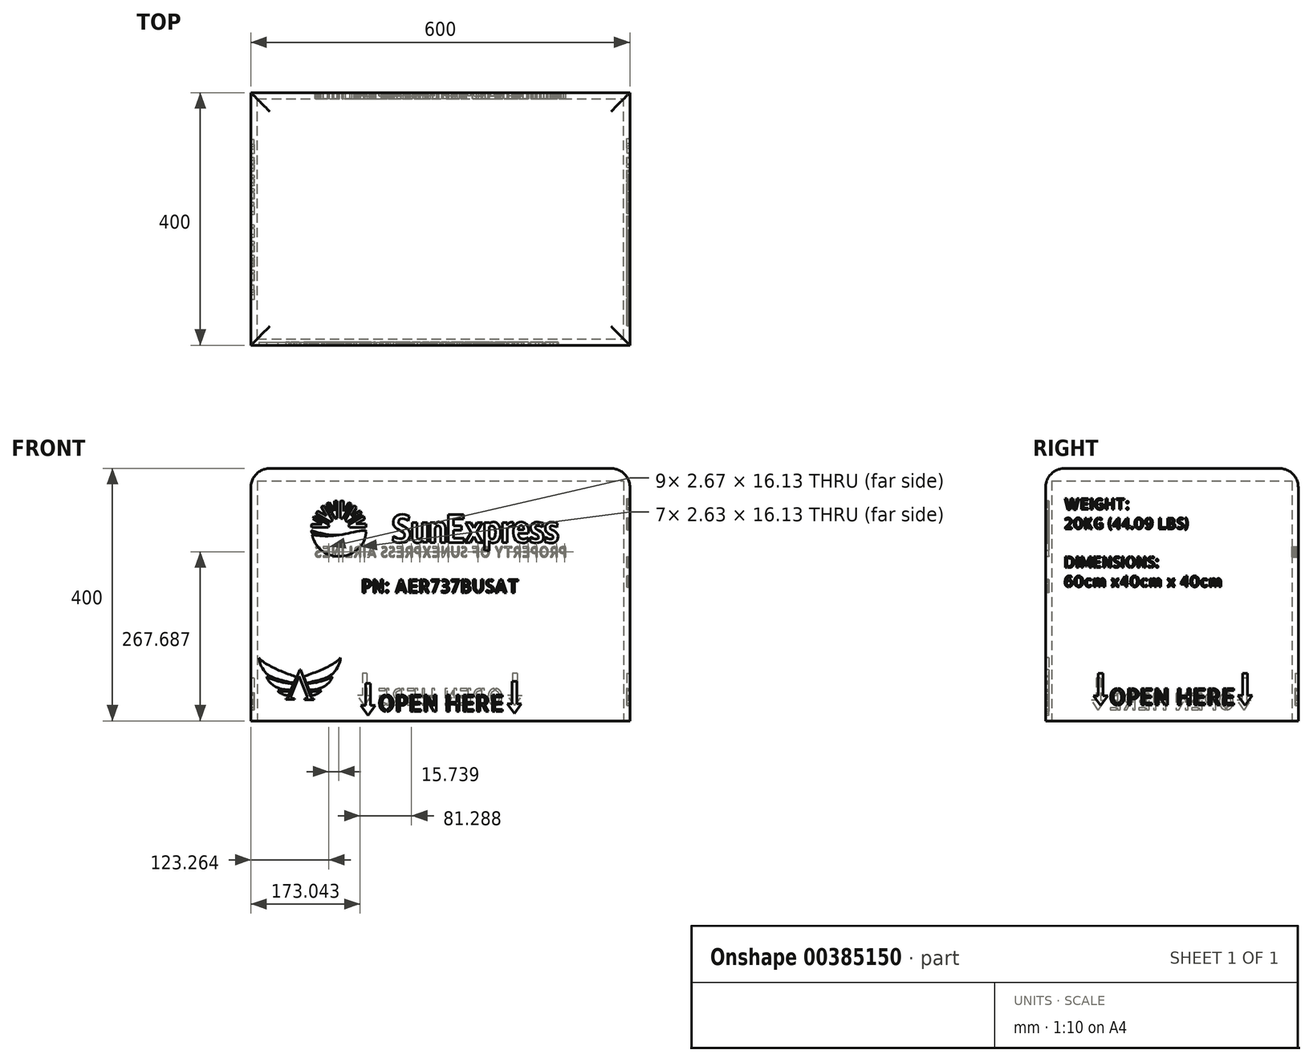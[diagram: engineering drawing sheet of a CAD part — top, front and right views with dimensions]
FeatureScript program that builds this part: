
annotation { "Feature Type Name" : "Feature", "Feature Type Description" : "" }
export const myFeature = defineFeature(function(context is Context, id is Id, definition is map)
    precondition{}
    {
        {
            var Q0;
            Q0=qCreatedBy(makeId("Top.planeOp"),FACE);
            var sketch = newSketch(context, id + "F0", { "sketchPlane" : qUnion([Q0])});
            skLineSegment(sketch, "E0.bottom", {"start": v(300, 200) * mm, "end": v(-300, 200) * mm});
            skLineSegment(sketch, "E0.top", {"start": v(300, -200) * mm, "end": v(-300, -200) * mm});
            skLineSegment(sketch, "E0.left", {"start": v(300, 200) * mm, "end": v(300, -200) * mm});
            skLineSegment(sketch, "E0.right", {"start": v(-300, 200) * mm, "end": v(-300, -200) * mm});
            skPoint(sketch, "E0.middle", {"position": v(0, 0) * mm});
            skSolve(sketch);
        }
        {
            var Q0;
            Q0=makeQuery(id+"F0.imprint","IMPRINT",FACE,{"disambiguationData":[TD([[makeQuery(id+"F0.imprint","IMPRINT",EDGE,{"derivedFrom":sQuery(id+"F0.wireOp",EDGE,"E0.bottom")}),1.0]])]});
            extrude(context, id + "F1", {"entities" : qUnion([Q0]), "oppositeDirection" : true, "depth" : 400 * mm});
        }
        {
            var Q0;
            Q0=makeQuery(id+"F1.opExtrude","CAP_FACE",FACE,{"disambiguationData":[OSD([sQuery(id+"F0.wireOp",EDGE,"E0.bottom"),sQuery(id+"F0.wireOp",EDGE,"E0.top"),sQuery(id+"F0.wireOp",EDGE,"E0.left"),sQuery(id+"F0.wireOp",EDGE,"E0.right")])],"isStart":false});
            var sketch = newSketch(context, id + "F2", { "sketchPlane" : qUnion([Q0])});
            skLineSegment(sketch, "E1.bottom", {"start": v(-290, 190) * mm, "end": v(290, 190) * mm});
            skLineSegment(sketch, "E1.top", {"start": v(-290, -190) * mm, "end": v(290, -190) * mm});
            skLineSegment(sketch, "E1.left", {"start": v(-290, 190) * mm, "end": v(-290, -190) * mm});
            skLineSegment(sketch, "E1.right", {"start": v(290, 190) * mm, "end": v(290, -190) * mm});
            skPoint(sketch, "E1.middle", {"position": v(0, 0) * mm});
            skSolve(sketch);
        }
        {
            var Q0;
            Q0 = qSketchRegion(id + "F2", true);
            extrude(context, id + "F3", {"entities" : qUnion([Q0]), "operationType" : NewBodyOperationType.REMOVE, "oppositeDirection" : true, "depth" : 380 * mm});
        }
        {
            var Q0;
            Q0=makeQuery(id+"F1.opExtrude","CAP_EDGE",EDGE,{"disambiguationData":[OSD([sQuery(id+"F0.wireOp",EDGE,"E0.right")])],"isStart":true});
            var Q1;
            Q1=makeQuery(id+"F1.opExtrude","CAP_EDGE",EDGE,{"disambiguationData":[OSD([sQuery(id+"F0.wireOp",EDGE,"E0.top")])],"isStart":true});
            var Q2;
            Q2=makeQuery(id+"F1.opExtrude","CAP_EDGE",EDGE,{"disambiguationData":[OSD([sQuery(id+"F0.wireOp",EDGE,"E0.left")])],"isStart":true});
            var Q3;
            Q3=makeQuery(id+"F1.opExtrude","CAP_EDGE",EDGE,{"disambiguationData":[OSD([sQuery(id+"F0.wireOp",EDGE,"E0.bottom")])],"isStart":true});
            fillet(context, id + "F4", {"entities" : qUnion([Q0, Q1, Q2, Q3]), "radius" : 30 * mm, "tangentPropagation" : true, "allowEdgeOverflow" : false});
        }
        {
            var Q0;
            Q0=makeQuery(id+"F1.opExtrude","SWEPT_FACE",FACE,{"disambiguationData":[OSD([sQuery(id+"F0.wireOp",EDGE,"E0.top")])]});
            var sketch = newSketch(context, id + "F5", { "sketchPlane" : qUnion([Q0])});
            skText(sketch, "E2", { "text": "PN: AER737BUSAT", "fontName": "AllertaStencil-Regular.ttf"});
            const initialGuessF5  = {"E2": [-0.12502, -0.19671, 1, 0, 0.02039]};
            skSetInitialGuess(sketch, initialGuessF5);
            skSolve(sketch);
        }
        {
            var Q0;
            Q0 = qSketchRegion(id + "F5", true);
            extrude(context, id + "F6", {"entities" : qUnion([Q0]), "operationType" : NewBodyOperationType.REMOVE, "oppositeDirection" : true, "depth" : 5 * mm});
        }
        {
            var Q0;
            Q0=makeQuery(id+"F1.opExtrude","SWEPT_FACE",FACE,{"disambiguationData":[OSD([sQuery(id+"F0.wireOp",EDGE,"E0.bottom")])]});
            var sketch = newSketch(context, id + "F7", { "sketchPlane" : qUnion([Q0])});
            skText(sketch, "E3", { "text": "PROPERTY OF SUNEXPRESS AIRLINES", "fontName": "AllertaStencil-Regular.ttf"});
            const initialGuessF7  = {"E3": [-0.2002, -0.14038, 1, 0, 0.01614]};
            skSetInitialGuess(sketch, initialGuessF7);
            skSolve(sketch);
        }
        {
            var Q0;
            Q0 = qSketchRegion(id + "F7", true);
            var Q1;
            Q1 = qConstructionFilter(qBodyType(qCreatedBy(id + "F7" ,EDGE), BodyType.WIRE), ConstructionObject.NO);
            extrude(context, id + "F8", {"entities" : qUnion([Q0]), "operationType" : NewBodyOperationType.REMOVE, "surfaceEntities" : qUnion([Q1]), "oppositeDirection" : true, "depth" : 25 * mm});
        }
        {
            var Q0;
            Q0=makeQuery(id+"F1.opExtrude","SWEPT_FACE",FACE,{"disambiguationData":[OSD([sQuery(id+"F0.wireOp",EDGE,"E0.left")])]});
            var sketch = newSketch(context, id + "F9", { "sketchPlane" : qUnion([Q0])});
            skText(sketch, "E4", { "text": "WEIGHT:\n20KG (44.09 LBS)\n\nDIMENSIONS:\n60cm x40cm x 40cm\n", "fontName": "AllertaStencil-Regular.ttf"});
            const initialGuessF9  = {"E4": [-0.17095, -0.0652, 1, 0, 0.01723]};
            skSetInitialGuess(sketch, initialGuessF9);
            skSolve(sketch);
        }
        {
            var Q0;
            Q0 = qSketchRegion(id + "F9", true);
            extrude(context, id + "F10", {"entities" : qUnion([Q0]), "operationType" : NewBodyOperationType.REMOVE, "oppositeDirection" : true, "depth" : 5 * mm});
        }
        {
            var Q0;
            Q0=makeQuery(id+"F1.opExtrude","SWEPT_FACE",FACE,{"disambiguationData":[OSD([sQuery(id+"F0.wireOp",EDGE,"E0.left")])]});
            var sketch = newSketch(context, id + "F11", { "sketchPlane" : qUnion([Q0])});
            skText(sketch, "E5", { "text": "OPEN HERE ", "fontName": "AllertaStencil-Regular.ttf"});
            const initialGuessF11  = {"E5": [-0.09974, -0.37501, 1, 0, 0.02609]};
            skSetInitialGuess(sketch, initialGuessF11);
            skSolve(sketch);
        }
        {
            var Q0;
            Q0 = qSketchRegion(id + "F11", true);
            extrude(context, id + "F12", {"entities" : qUnion([Q0]), "operationType" : NewBodyOperationType.REMOVE, "oppositeDirection" : true, "depth" : 5 * mm});
        }
        {
            var Q0;
            Q0=makeQuery(id+"F1.opExtrude","SWEPT_FACE",FACE,{"disambiguationData":[OSD([sQuery(id+"F0.wireOp",EDGE,"E0.bottom")])]});
            var sketch = newSketch(context, id + "F13", { "sketchPlane" : qUnion([Q0])});
            skText(sketch, "E6", { "text": "OPEN HERE", "fontName": "AllertaStencil-Regular.ttf"});
            const initialGuessF13  = {"E6": [-0.1, -0.375, 1, 0, 0.02609]};
            skSetInitialGuess(sketch, initialGuessF13);
            skSolve(sketch);
        }
        {
            var Q0;
            Q0 = qSketchRegion(id + "F13", true);
            var Q1;
            Q1 = qConstructionFilter(qBodyType(qCreatedBy(id + "F13" ,EDGE), BodyType.WIRE), ConstructionObject.NO);
            extrude(context, id + "F14", {"entities" : qUnion([Q0]), "operationType" : NewBodyOperationType.REMOVE, "surfaceEntities" : qUnion([Q1]), "oppositeDirection" : true, "depth" : 5 * mm});
        }
        {
            var Q0;
            Q0=makeQuery(id+"F1.opExtrude","SWEPT_FACE",FACE,{"disambiguationData":[OSD([sQuery(id+"F0.wireOp",EDGE,"E0.right")])]});
            var sketch = newSketch(context, id + "F15", { "sketchPlane" : qUnion([Q0])});
            skText(sketch, "E7", { "text": "OPEN HERE", "fontName": "AllertaStencil-Regular.ttf"});
            const initialGuessF15  = {"E7": [-0.09969, -0.38217, 1, 0, 0.02609]};
            skSetInitialGuess(sketch, initialGuessF15);
            skSolve(sketch);
        }
        {
            var Q0;
            Q0 = qSketchRegion(id + "F15", true);
            extrude(context, id + "F16", {"entities" : qUnion([Q0]), "operationType" : NewBodyOperationType.REMOVE, "oppositeDirection" : true, "depth" : 5 * mm});
        }
        {
            var Q0;
            Q0=makeQuery(id+"F1.opExtrude","SWEPT_FACE",FACE,{"disambiguationData":[OSD([sQuery(id+"F0.wireOp",EDGE,"E0.top")])]});
            var sketch = newSketch(context, id + "F17", { "sketchPlane" : qUnion([Q0])});
            skText(sketch, "E8", { "text": "OPEN HERE", "fontName": "AllertaStencil-Regular.ttf"});
            const initialGuessF17  = {"E8": [-0.09926, -0.38504, 1, 0, 0.02609]};
            skSetInitialGuess(sketch, initialGuessF17);
            skSolve(sketch);
        }
        {
            var Q0;
            Q0 = qSketchRegion(id + "F17", true);
            extrude(context, id + "F18", {"entities" : qUnion([Q0]), "operationType" : NewBodyOperationType.REMOVE, "oppositeDirection" : true, "depth" : 5 * mm});
        }
        {
            var Q0;
            Q0=makeQuery(id+"F1.opExtrude","SWEPT_FACE",FACE,{"disambiguationData":[OSD([sQuery(id+"F0.wireOp",EDGE,"E0.top")])]});
            var sketch = newSketch(context, id + "F19", { "sketchPlane" : qUnion([Q0])});
            skLineSegment(sketch, "E9", {"start": v(113.26, -337.65) * mm, "end": v(120.76, -337.65) * mm});
            skLineSegment(sketch, "E10", {"start": v(120.76, -337.65) * mm, "end": v(120.76, -372.65) * mm});
            skLineSegment(sketch, "E11", {"start": v(120.76, -372.65) * mm, "end": v(128.26, -372.65) * mm});
            skPoint(sketch, "E12.endSnap0", {"position": v(117, -337.65) * mm});
            skLineSegment(sketch, "E13", {"start": v(113.26, -337.65) * mm, "end": v(113.26, -372.65) * mm});
            skLineSegment(sketch, "E14", {"start": v(113.26, -372.65) * mm, "end": v(105.76, -372.65) * mm});
            skLineSegment(sketch, "E15", {"start": v(117, -388.42) * mm, "end": v(105.76, -372.65) * mm});
            skLineSegment(sketch, "E16", {"start": v(117, -388.42) * mm, "end": v(128.26, -372.65) * mm});
            skLineSegment(sketch, "E17", {"start": v(-118.37, -340.6) * mm, "end": v(-110.87, -340.6) * mm});
            skLineSegment(sketch, "E18", {"start": v(-110.87, -340.6) * mm, "end": v(-110.87, -375.6) * mm});
            skLineSegment(sketch, "E19", {"start": v(-110.87, -375.6) * mm, "end": v(-103.37, -375.6) * mm});
            skPoint(sketch, "E20.endSnap0", {"position": v(-114.62, -340.6) * mm});
            skLineSegment(sketch, "E21", {"start": v(-118.37, -340.6) * mm, "end": v(-118.37, -375.6) * mm});
            skLineSegment(sketch, "E22", {"start": v(-118.37, -375.6) * mm, "end": v(-125.87, -375.6) * mm});
            skLineSegment(sketch, "E23", {"start": v(-114.62, -391.38) * mm, "end": v(-125.87, -375.6) * mm});
            skLineSegment(sketch, "E24", {"start": v(-114.62, -391.38) * mm, "end": v(-103.37, -375.6) * mm});
            skSolve(sketch);
        }
        {
            var Q0;
            Q0=makeQuery(id+"F19.imprint","IMPRINT",FACE,{"disambiguationData":[TD([[makeQuery(id+"F19.imprint","IMPRINT",EDGE,{"derivedFrom":sQuery(id+"F19.wireOp",EDGE,"E9")}),-1.0]])]});
            var Q1;
            Q1=makeQuery(id+"F19.imprint","IMPRINT",FACE,{"disambiguationData":[TD([[makeQuery(id+"F19.imprint","IMPRINT",EDGE,{"derivedFrom":sQuery(id+"F19.wireOp",EDGE,"E17")}),-1.0]])]});
            extrude(context, id + "F20", {"entities" : qUnion([Q0, Q1]), "operationType" : NewBodyOperationType.REMOVE, "oppositeDirection" : true, "depth" : 5 * mm});
        }
        {
            var Q0;
            Q0=makeQuery(id+"F1.opExtrude","SWEPT_FACE",FACE,{"disambiguationData":[OSD([sQuery(id+"F0.wireOp",EDGE,"E0.left")])]});
            var sketch = newSketch(context, id + "F21", { "sketchPlane" : qUnion([Q0])});
            skLineSegment(sketch, "E25", {"start": v(112.16, -324.4) * mm, "end": v(119.66, -324.4) * mm});
            skLineSegment(sketch, "E26", {"start": v(119.66, -324.4) * mm, "end": v(119.66, -359.4) * mm});
            skLineSegment(sketch, "E27", {"start": v(119.66, -359.4) * mm, "end": v(127.16, -359.4) * mm});
            skPoint(sketch, "E28.endSnap0", {"position": v(115.91, -324.4) * mm});
            skLineSegment(sketch, "E29", {"start": v(112.16, -324.4) * mm, "end": v(112.16, -359.4) * mm});
            skLineSegment(sketch, "E30", {"start": v(112.16, -359.4) * mm, "end": v(104.66, -359.4) * mm});
            skLineSegment(sketch, "E31", {"start": v(115.91, -375.17) * mm, "end": v(104.66, -359.4) * mm});
            skLineSegment(sketch, "E32", {"start": v(115.91, -375.17) * mm, "end": v(127.16, -359.4) * mm});
            skLineSegment(sketch, "E33", {"start": v(-116.57, -324.94) * mm, "end": v(-109.07, -324.94) * mm});
            skLineSegment(sketch, "E34", {"start": v(-109.07, -324.94) * mm, "end": v(-109.07, -359.94) * mm});
            skLineSegment(sketch, "E35", {"start": v(-109.07, -359.94) * mm, "end": v(-101.57, -359.94) * mm});
            skPoint(sketch, "E36.endSnap0", {"position": v(-112.82, -324.94) * mm});
            skLineSegment(sketch, "E37", {"start": v(-116.57, -324.94) * mm, "end": v(-116.57, -359.94) * mm});
            skLineSegment(sketch, "E38", {"start": v(-116.57, -359.94) * mm, "end": v(-124.07, -359.94) * mm});
            skLineSegment(sketch, "E39", {"start": v(-112.82, -375.72) * mm, "end": v(-124.07, -359.94) * mm});
            skLineSegment(sketch, "E40", {"start": v(-112.82, -375.72) * mm, "end": v(-101.57, -359.94) * mm});
            skSolve(sketch);
        }
        {
            var Q0;
            Q0 = qSketchRegion(id + "F21", true);
            extrude(context, id + "F22", {"entities" : qUnion([Q0]), "operationType" : NewBodyOperationType.REMOVE, "oppositeDirection" : true, "depth" : 5 * mm});
        }
        {
            var Q0;
            Q0=makeQuery(id+"F1.opExtrude","SWEPT_FACE",FACE,{"disambiguationData":[OSD([sQuery(id+"F0.wireOp",EDGE,"E0.bottom")])]});
            var sketch = newSketch(context, id + "F23", { "sketchPlane" : qUnion([Q0])});
            skLineSegment(sketch, "E41", {"start": v(116.23, -324.57) * mm, "end": v(123.73, -324.57) * mm});
            skLineSegment(sketch, "E42", {"start": v(123.73, -324.57) * mm, "end": v(123.73, -359.57) * mm});
            skLineSegment(sketch, "E43", {"start": v(123.73, -359.57) * mm, "end": v(131.23, -359.57) * mm});
            skPoint(sketch, "E44.endSnap0", {"position": v(119.98, -324.57) * mm});
            skLineSegment(sketch, "E45", {"start": v(116.23, -324.57) * mm, "end": v(116.23, -359.57) * mm});
            skLineSegment(sketch, "E46", {"start": v(116.23, -359.57) * mm, "end": v(108.73, -359.57) * mm});
            skLineSegment(sketch, "E47", {"start": v(119.98, -375.34) * mm, "end": v(108.73, -359.57) * mm});
            skLineSegment(sketch, "E48", {"start": v(119.98, -375.34) * mm, "end": v(131.23, -359.57) * mm});
            skLineSegment(sketch, "E49", {"start": v(-121.59, -324.57) * mm, "end": v(-114.09, -324.57) * mm});
            skLineSegment(sketch, "E50", {"start": v(-114.09, -324.57) * mm, "end": v(-114.09, -359.57) * mm});
            skLineSegment(sketch, "E51", {"start": v(-114.09, -359.57) * mm, "end": v(-106.59, -359.57) * mm});
            skPoint(sketch, "E52.endSnap0", {"position": v(-117.84, -324.57) * mm});
            skLineSegment(sketch, "E53", {"start": v(-121.59, -324.57) * mm, "end": v(-121.59, -359.57) * mm});
            skLineSegment(sketch, "E54", {"start": v(-121.59, -359.57) * mm, "end": v(-129.09, -359.57) * mm});
            skLineSegment(sketch, "E55", {"start": v(-117.84, -375.34) * mm, "end": v(-129.09, -359.57) * mm});
            skLineSegment(sketch, "E56", {"start": v(-117.84, -375.34) * mm, "end": v(-106.59, -359.57) * mm});
            skSolve(sketch);
        }
        {
            var Q0;
            Q0 = qSketchRegion(id + "F23", true);
            extrude(context, id + "F24", {"entities" : qUnion([Q0]), "operationType" : NewBodyOperationType.REMOVE, "oppositeDirection" : true, "depth" : 5 * mm});
        }
        {
            var Q0;
            Q0=makeQuery(id+"F1.opExtrude","SWEPT_FACE",FACE,{"disambiguationData":[OSD([sQuery(id+"F0.wireOp",EDGE,"E0.right")])]});
            var sketch = newSketch(context, id + "F25", { "sketchPlane" : qUnion([Q0])});
            skLineSegment(sketch, "E57", {"start": v(112.6, -331.98) * mm, "end": v(120.1, -331.98) * mm});
            skLineSegment(sketch, "E58", {"start": v(120.1, -331.98) * mm, "end": v(120.1, -366.98) * mm});
            skLineSegment(sketch, "E59", {"start": v(120.1, -366.98) * mm, "end": v(127.6, -366.98) * mm});
            skPoint(sketch, "E60.endSnap0", {"position": v(116.35, -331.98) * mm});
            skLineSegment(sketch, "E61", {"start": v(112.6, -331.98) * mm, "end": v(112.6, -366.98) * mm});
            skLineSegment(sketch, "E62", {"start": v(112.6, -366.98) * mm, "end": v(105.1, -366.98) * mm});
            skLineSegment(sketch, "E63", {"start": v(116.35, -382.75) * mm, "end": v(105.1, -366.98) * mm});
            skLineSegment(sketch, "E64", {"start": v(116.35, -382.75) * mm, "end": v(127.6, -366.98) * mm});
            skLineSegment(sketch, "E65", {"start": v(-118.05, -331.98) * mm, "end": v(-110.55, -331.98) * mm});
            skLineSegment(sketch, "E66", {"start": v(-110.55, -331.98) * mm, "end": v(-110.55, -366.98) * mm});
            skLineSegment(sketch, "E67", {"start": v(-110.55, -366.98) * mm, "end": v(-103.05, -366.98) * mm});
            skPoint(sketch, "E68.endSnap0", {"position": v(-114.3, -331.98) * mm});
            skLineSegment(sketch, "E69", {"start": v(-118.05, -331.98) * mm, "end": v(-118.05, -366.98) * mm});
            skLineSegment(sketch, "E70", {"start": v(-118.05, -366.98) * mm, "end": v(-125.55, -366.98) * mm});
            skLineSegment(sketch, "E71", {"start": v(-114.3, -382.75) * mm, "end": v(-125.55, -366.98) * mm});
            skLineSegment(sketch, "E72", {"start": v(-114.3, -382.75) * mm, "end": v(-103.05, -366.98) * mm});
            skSolve(sketch);
        }
        {
            var Q0;
            Q0=makeQuery(id+"F25.imprint","IMPRINT",FACE,{"disambiguationData":[TD([[makeQuery(id+"F25.imprint","IMPRINT",EDGE,{"derivedFrom":sQuery(id+"F25.wireOp",EDGE,"E65")}),-1.0]])]});
            var Q1;
            Q1=makeQuery(id+"F25.imprint","IMPRINT",FACE,{"disambiguationData":[TD([[makeQuery(id+"F25.imprint","IMPRINT",EDGE,{"derivedFrom":sQuery(id+"F25.wireOp",EDGE,"E57")}),-1.0]])]});
            extrude(context, id + "F26", {"entities" : qUnion([Q0, Q1]), "operationType" : NewBodyOperationType.REMOVE, "oppositeDirection" : true, "depth" : 5 * mm});
        }
        {
            var Q0;
            Q0=makeQuery(id+"F1.opExtrude","SWEPT_FACE",FACE,{"disambiguationData":[OSD([sQuery(id+"F0.wireOp",EDGE,"E0.top")])]});
            var sketch = newSketch(context, id + "F27", { "sketchPlane" : qUnion([Q0])});
            skFitSpline(sketch, "E73", {"points": [v(-287.47, -300.17) * mm, v(-285.64, -307.65) * mm, v(-282.97, -314.34) * mm, v(-277.16, -323.03) * mm, v(-270.08, -328.64) * mm, v(-258.87, -333.26) * mm, v(-248.85, -336.14) * mm, v(-236.1, -339.08) * mm, v(-231.97, -339.77) * mm], "startDerivative": vector(14.73, -66.56) * mm, "endDerivative": vector(37.86, -4.5) * mm});
            skFitSpline(sketch, "E74", {"points": [v(-287.47, -300.17) * mm, v(-280.7, -306.24) * mm, v(-272.35, -311.5) * mm, v(-262.68, -316.6) * mm, v(-254.9, -320.18) * mm, v(-244.88, -324.1) * mm, v(-235, -327.89) * mm, v(-227.87, -330.32) * mm], "startDerivative": vector(46.83, -45.33) * mm, "endDerivative": vector(52.79, -17.03) * mm});
            skFitSpline(sketch, "E75", {"points": [v(-275.38, -329.68) * mm, v(-272.8, -334.93) * mm, v(-268.97, -339.85) * mm, v(-263.38, -344.43) * mm, v(-255.22, -348.27) * mm, v(-243.8, -350.68) * mm, v(-236.84, -351.02) * mm], "startDerivative": vector(16.29, -36.96) * mm, "endDerivative": vector(41.84, -0.26) * mm});
            skFitSpline(sketch, "E76", {"points": [v(-275.38, -329.68) * mm, v(-269.47, -332.6) * mm, v(-260.88, -335.85) * mm, v(-252.8, -338.18) * mm, v(-242.55, -340.18) * mm, v(-232.77, -341.62) * mm], "startDerivative": vector(32.04, -16.82) * mm, "endDerivative": vector(44.27, -6.3) * mm});
            skFitSpline(sketch, "E77", {"points": [v(-257.64, -352) * mm, v(-254.14, -355.29) * mm, v(-248.11, -358.3) * mm, v(-242.3, -359.56) * mm, v(-240.54, -359.56) * mm], "startDerivative": vector(12.37, -13.28) * mm, "endDerivative": vector(9.63, 0.61) * mm});
            skFitSpline(sketch, "E78", {"points": [v(-257.64, -352) * mm, v(-251.62, -352.83) * mm, v(-245.6, -353.32) * mm, v(-239.7, -353.4) * mm, v(-237.84, -353.32) * mm], "startDerivative": vector(21.45, -3.2) * mm, "endDerivative": vector(9.92, 0.53) * mm});
            skLineSegment(sketch, "E79", {"start": v(-204.23, -359.6) * mm, "end": v(-206.68, -353.37) * mm});
            skFitSpline(sketch, "E80", {"points": [v(-158.12, -300.1) * mm, v(-163.54, -305.05) * mm, v(-170.37, -309.88) * mm, v(-180.5, -315.3) * mm, v(-190.3, -319.9) * mm, v(-202.43, -324.61) * mm, v(-212.1, -328.38) * mm, v(-215.86, -330.03) * mm], "startDerivative": vector(-41.21, -39.44) * mm, "endDerivative": vector(-34.78, -15.75) * mm});
            skFitSpline(sketch, "E81", {"points": [v(-158.12, -300.1) * mm, v(-159.65, -307.64) * mm, v(-163.3, -315.9) * mm, v(-169.43, -324.38) * mm, v(-173.8, -327.56) * mm, v(-180.04, -330.98) * mm, v(-186.64, -333.69) * mm, v(-192.65, -335.46) * mm, v(-202.78, -337.81) * mm, v(-212.07, -339.68) * mm], "startDerivative": vector(-10.94, -69.54) * mm, "endDerivative": vector(-74.54, -14.42) * mm});
            skFitSpline(sketch, "E82", {"points": [v(-170.41, -330.03) * mm, v(-174.06, -336.2) * mm, v(-178.05, -340.9) * mm, v(-182.75, -344.54) * mm, v(-186.6, -346.57) * mm, v(-191.71, -348.68) * mm, v(-198.02, -350.29) * mm, v(-207.73, -350.7) * mm], "startDerivative": vector(-23.37, -42.5) * mm, "endDerivative": vector(-58.2, -0.2) * mm});
            skFitSpline(sketch, "E83", {"points": [v(-170.41, -330.03) * mm, v(-176.3, -332.7) * mm, v(-183.66, -335.43) * mm, v(-193.26, -338.38) * mm, v(-201.18, -339.78) * mm, v(-211.46, -341.24) * mm], "startDerivative": vector(-33.05, -15.61) * mm, "endDerivative": vector(-48.47, -6.89) * mm});
            skLineSegment(sketch, "E84.trimOffspring", {"start": v(-212.07, -339.68) * mm, "end": v(-215.86, -330.03) * mm});
            skFitSpline(sketch, "E85", {"points": [v(-188.1, -351.95) * mm, v(-193.65, -356.41) * mm, v(-199.9, -359.09) * mm, v(-204.23, -359.6) * mm], "startDerivative": vector(-14.5, -13.16) * mm, "endDerivative": vector(-14.58, -0.68) * mm});
            skFitSpline(sketch, "E86", {"points": [v(-188.1, -351.95) * mm, v(-194.55, -352.94) * mm, v(-199.4, -353.44) * mm, v(-204.23, -353.54) * mm, v(-206.68, -353.37) * mm], "startDerivative": vector(-22.43, -3.62) * mm, "endDerivative": vector(-12.06, 1.1) * mm});
            skLineSegment(sketch, "E87.trimOffspring", {"start": v(-207.73, -350.7) * mm, "end": v(-211.46, -341.24) * mm});
            skLineSegment(sketch, "E88", {"start": v(-240.54, -359.56) * mm, "end": v(-237.84, -353.32) * mm});
            skLineSegment(sketch, "E89.trimOffspring", {"start": v(-231.97, -339.77) * mm, "end": v(-227.87, -330.32) * mm});
            skLineSegment(sketch, "E90.trimOffspring", {"start": v(-236.84, -351.02) * mm, "end": v(-232.77, -341.62) * mm});
            skLineSegment(sketch, "E91", {"start": v(-239.23, -360.06) * mm, "end": v(-222.17, -318.74) * mm});
            skLineSegment(sketch, "E92", {"start": v(-222.17, -318.74) * mm, "end": v(-221.15, -318.74) * mm});
            skLineSegment(sketch, "E93", {"start": v(-221.15, -318.74) * mm, "end": v(-205.95, -360) * mm});
            skLineSegment(sketch, "E94", {"start": v(-223.7, -328.86) * mm, "end": v(-236.54, -360.55) * mm});
            skLineSegment(sketch, "E95", {"start": v(-223.7, -328.86) * mm, "end": v(-211.3, -360.72) * mm});
            skLineSegment(sketch, "E96", {"start": v(-244.84, -364.89) * mm, "end": v(-244.84, -366.15) * mm});
            skLineSegment(sketch, "E97", {"start": v(-244.84, -366.15) * mm, "end": v(-230.97, -366.15) * mm});
            skLineSegment(sketch, "E98", {"start": v(-230.97, -366.15) * mm, "end": v(-230.9, -364.89) * mm});
            skLineSegment(sketch, "E99", {"start": v(-214.7, -364.96) * mm, "end": v(-214.7, -366.29) * mm});
            skLineSegment(sketch, "E100", {"start": v(-214.7, -366.29) * mm, "end": v(-200.13, -366.29) * mm});
            skLineSegment(sketch, "E101", {"start": v(-200.13, -366.29) * mm, "end": v(-200.13, -364.68) * mm});
            skFitSpline(sketch, "E102", {"points": [v(-239.23, -360.06) * mm, v(-240.36, -362.22) * mm, v(-241.97, -363.9) * mm, v(-244.84, -364.89) * mm], "startDerivative": vector(-3.24, -6.88) * mm, "endDerivative": vector(-8.66, -2.08) * mm});
            skFitSpline(sketch, "E103", {"points": [v(-236.54, -360.55) * mm, v(-236.79, -361.65) * mm, v(-236.2, -363.16) * mm, v(-234.36, -364.18) * mm, v(-230.9, -364.89) * mm], "startDerivative": vector(-2.04, -5.52) * mm, "endDerivative": vector(11.11, -1.85) * mm});
            skFitSpline(sketch, "E104", {"points": [v(-211.3, -360.72) * mm, v(-211, -362.04) * mm, v(-210.97, -363.27) * mm, v(-211.7, -364.16) * mm, v(-213.24, -364.6) * mm, v(-214.7, -364.96) * mm], "startDerivative": vector(1.59, -6.6) * mm, "endDerivative": vector(-6.8, -1.78) * mm});
            skFitSpline(sketch, "E105", {"points": [v(-205.95, -360) * mm, v(-205.25, -361.45) * mm, v(-204.43, -362.95) * mm, v(-203.19, -364.19) * mm, v(-201.75, -364.54) * mm, v(-200.13, -364.68) * mm], "startDerivative": vector(3.47, -7.3) * mm, "endDerivative": vector(8.17, -0.63) * mm});
            skLineSegment(sketch, "E106", {"start": v(-201, -80.25) * mm, "end": v(-201.3, -79.66) * mm});
            skLineSegment(sketch, "E107", {"start": v(-201.3, -79.66) * mm, "end": v(-199.65, -76.18) * mm});
            skLineSegment(sketch, "E108", {"start": v(-199.65, -76.18) * mm, "end": v(-198.6, -76.1) * mm});
            skLineSegment(sketch, "E109", {"start": v(-198.6, -76.1) * mm, "end": v(-176.66, -88.87) * mm});
            skLineSegment(sketch, "E110", {"start": v(-176.66, -88.87) * mm, "end": v(-176.17, -89.8) * mm});
            skLineSegment(sketch, "E111", {"start": v(-176.17, -89.8) * mm, "end": v(-176.81, -92.38) * mm});
            skLineSegment(sketch, "E112", {"start": v(-176.81, -92.38) * mm, "end": v(-177.45, -93.23) * mm});
            skLineSegment(sketch, "E113", {"start": v(-177.45, -93.23) * mm, "end": v(-203.22, -93.23) * mm});
            skLineSegment(sketch, "E114", {"start": v(-203.22, -93.23) * mm, "end": v(-203.96, -92.43) * mm});
            skLineSegment(sketch, "E115", {"start": v(-203.96, -92.43) * mm, "end": v(-203.96, -89.06) * mm});
            skLineSegment(sketch, "E116", {"start": v(-203.96, -89.06) * mm, "end": v(-203.17, -88.22) * mm});
            skLineSegment(sketch, "E117", {"start": v(-203.17, -88.22) * mm, "end": v(-187.81, -88.22) * mm});
            skLineSegment(sketch, "E118", {"start": v(-187.81, -88.22) * mm, "end": v(-201, -80.25) * mm});
            skLineSegment(sketch, "E119", {"start": v(-196.59, -71.78) * mm, "end": v(-174.59, -84.66) * mm});
            skLineSegment(sketch, "E120", {"start": v(-174.59, -84.66) * mm, "end": v(-173.34, -84.57) * mm});
            skLineSegment(sketch, "E121", {"start": v(-173.34, -84.57) * mm, "end": v(-171.25, -82.74) * mm});
            skLineSegment(sketch, "E122", {"start": v(-171.25, -82.74) * mm, "end": v(-171.17, -81.82) * mm});
            skLineSegment(sketch, "E123", {"start": v(-171.17, -81.82) * mm, "end": v(-183.76, -59.6) * mm});
            skLineSegment(sketch, "E124", {"start": v(-183.76, -59.6) * mm, "end": v(-184.7, -58.88) * mm});
            skLineSegment(sketch, "E125", {"start": v(-184.7, -58.88) * mm, "end": v(-188, -61.06) * mm});
            skLineSegment(sketch, "E126", {"start": v(-188, -61.06) * mm, "end": v(-188, -62) * mm});
            skLineSegment(sketch, "E127", {"start": v(-188, -62) * mm, "end": v(-180.73, -75.19) * mm});
            skLineSegment(sketch, "E128", {"start": v(-180.73, -75.19) * mm, "end": v(-193.46, -67.84) * mm});
            skLineSegment(sketch, "E129", {"start": v(-193.46, -67.84) * mm, "end": v(-194.54, -67.93) * mm});
            skLineSegment(sketch, "E130", {"start": v(-194.54, -67.93) * mm, "end": v(-196.67, -70.67) * mm});
            skLineSegment(sketch, "E131", {"start": v(-196.67, -70.67) * mm, "end": v(-196.59, -71.78) * mm});
            skLineSegment(sketch, "E132", {"start": v(-179.98, -57.34) * mm, "end": v(-166.93, -79.75) * mm});
            skLineSegment(sketch, "E133", {"start": v(-166.93, -79.75) * mm, "end": v(-166.18, -79.75) * mm});
            skLineSegment(sketch, "E134", {"start": v(-166.18, -79.75) * mm, "end": v(-163.72, -79.13) * mm});
            skLineSegment(sketch, "E135", {"start": v(-163.72, -79.13) * mm, "end": v(-163.1, -78.42) * mm});
            skLineSegment(sketch, "E136", {"start": v(-163.1, -78.42) * mm, "end": v(-163.1, -52.55) * mm});
            skLineSegment(sketch, "E137", {"start": v(-163.1, -52.55) * mm, "end": v(-163.62, -51.51) * mm});
            skLineSegment(sketch, "E138", {"start": v(-163.62, -51.51) * mm, "end": v(-167.44, -51.79) * mm});
            skLineSegment(sketch, "E139", {"start": v(-167.44, -51.79) * mm, "end": v(-168.14, -52.58) * mm});
            skLineSegment(sketch, "E140", {"start": v(-168.14, -52.58) * mm, "end": v(-168.14, -67.7) * mm});
            skLineSegment(sketch, "E141", {"start": v(-168.14, -67.7) * mm, "end": v(-175.46, -54.67) * mm});
            skLineSegment(sketch, "E142", {"start": v(-175.46, -54.67) * mm, "end": v(-176.16, -54.23) * mm});
            skLineSegment(sketch, "E143", {"start": v(-176.16, -54.23) * mm, "end": v(-179.92, -55.86) * mm});
            skLineSegment(sketch, "E144", {"start": v(-179.98, -57.34) * mm, "end": v(-179.92, -55.86) * mm});
            skLineSegment(sketch, "E145", {"start": v(-158.5, -78.26) * mm, "end": v(-158.5, -52.33) * mm});
            skLineSegment(sketch, "E146", {"start": v(-158.5, -52.33) * mm, "end": v(-157.7, -51.37) * mm});
            skLineSegment(sketch, "E147", {"start": v(-157.7, -51.37) * mm, "end": v(-154.16, -51.58) * mm});
            skLineSegment(sketch, "E148", {"start": v(-154.16, -51.58) * mm, "end": v(-153.32, -52.53) * mm});
            skLineSegment(sketch, "E149", {"start": v(-153.32, -52.53) * mm, "end": v(-153.32, -68.05) * mm});
            skLineSegment(sketch, "E150", {"start": v(-153.32, -68.05) * mm, "end": v(-145.83, -54.56) * mm});
            skLineSegment(sketch, "E151", {"start": v(-145.83, -54.56) * mm, "end": v(-145.05, -54.18) * mm});
            skLineSegment(sketch, "E152", {"start": v(-145.05, -54.18) * mm, "end": v(-141.48, -55.96) * mm});
            skLineSegment(sketch, "E153", {"start": v(-141.48, -55.96) * mm, "end": v(-141.2, -56.74) * mm});
            skLineSegment(sketch, "E154", {"start": v(-141.2, -56.74) * mm, "end": v(-154.5, -79.68) * mm});
            skLineSegment(sketch, "E155", {"start": v(-154.5, -79.68) * mm, "end": v(-155.12, -79.85) * mm});
            skLineSegment(sketch, "E156", {"start": v(-155.12, -79.85) * mm, "end": v(-157.67, -79.26) * mm});
            skLineSegment(sketch, "E157", {"start": v(-157.67, -79.26) * mm, "end": v(-158.5, -78.26) * mm});
            skLineSegment(sketch, "E158", {"start": v(-137.45, -59.32) * mm, "end": v(-150.2, -81.53) * mm});
            skLineSegment(sketch, "E159", {"start": v(-150.2, -81.53) * mm, "end": v(-150.12, -82.69) * mm});
            skLineSegment(sketch, "E160", {"start": v(-150.12, -82.69) * mm, "end": v(-147.98, -84.82) * mm});
            skLineSegment(sketch, "E161", {"start": v(-147.98, -84.82) * mm, "end": v(-147.07, -84.9) * mm});
            skLineSegment(sketch, "E162", {"start": v(-147.07, -84.9) * mm, "end": v(-125.14, -72.14) * mm});
            skLineSegment(sketch, "E163", {"start": v(-125.14, -72.14) * mm, "end": v(-124.4, -71.05) * mm});
            skLineSegment(sketch, "E164", {"start": v(-124.4, -71.05) * mm, "end": v(-126.65, -67.72) * mm});
            skLineSegment(sketch, "E165", {"start": v(-126.65, -67.72) * mm, "end": v(-127.94, -67.62) * mm});
            skLineSegment(sketch, "E166", {"start": v(-127.94, -67.62) * mm, "end": v(-141.19, -75.47) * mm});
            skLineSegment(sketch, "E167", {"start": v(-141.19, -75.47) * mm, "end": v(-133.16, -62.19) * mm});
            skLineSegment(sketch, "E168", {"start": v(-133.16, -62.19) * mm, "end": v(-133.3, -60.9) * mm});
            skLineSegment(sketch, "E169", {"start": v(-133.3, -60.9) * mm, "end": v(-136.5, -58.86) * mm});
            skLineSegment(sketch, "E170", {"start": v(-136.5, -58.86) * mm, "end": v(-137.44, -59.31) * mm});
            skLineSegment(sketch, "E171", {"start": v(-122.82, -75.84) * mm, "end": v(-144.9, -88.76) * mm});
            skLineSegment(sketch, "E172", {"start": v(-144.9, -88.76) * mm, "end": v(-145.4, -89.93) * mm});
            skLineSegment(sketch, "E173", {"start": v(-145.4, -89.93) * mm, "end": v(-144.66, -92.5) * mm});
            skLineSegment(sketch, "E174", {"start": v(-144.66, -92.5) * mm, "end": v(-143.49, -93.26) * mm});
            skLineSegment(sketch, "E175", {"start": v(-143.49, -93.26) * mm, "end": v(-118.32, -93.26) * mm});
            skLineSegment(sketch, "E176", {"start": v(-118.32, -93.26) * mm, "end": v(-117.54, -92.52) * mm});
            skLineSegment(sketch, "E177", {"start": v(-117.54, -92.52) * mm, "end": v(-117.54, -88.87) * mm});
            skLineSegment(sketch, "E178", {"start": v(-117.54, -88.87) * mm, "end": v(-118.57, -88.1) * mm});
            skLineSegment(sketch, "E179", {"start": v(-118.57, -88.1) * mm, "end": v(-133.49, -88.1) * mm});
            skLineSegment(sketch, "E180", {"start": v(-133.49, -88.1) * mm, "end": v(-120.32, -80.5) * mm});
            skLineSegment(sketch, "E181", {"start": v(-120.32, -80.5) * mm, "end": v(-119.99, -79.68) * mm});
            skLineSegment(sketch, "E182", {"start": v(-119.99, -79.68) * mm, "end": v(-121.66, -75.93) * mm});
            skLineSegment(sketch, "E183", {"start": v(-121.66, -75.93) * mm, "end": v(-122.82, -75.84) * mm});
            skFitSpline(sketch, "E184", {"points": [v(-202.88, -105.5) * mm, v(-201.76, -110) * mm, v(-199.52, -115.46) * mm, v(-194.75, -123.03) * mm, v(-187.04, -130.88) * mm, v(-179.34, -135.5) * mm, v(-168.96, -138.73) * mm, v(-156.91, -139.43) * mm, v(-143.74, -136.34) * mm, v(-133.79, -130.46) * mm, v(-125.8, -122.6) * mm, v(-120.75, -114.06) * mm, v(-118.37, -105.5) * mm, v(-117.39, -99.9) * mm], "startDerivative": vector(17.85, -81.63) * mm, "endDerivative": vector(14.13, 87.9) * mm});
            skFitSpline(sketch, "E185", {"points": [v(-117.39, -99.9) * mm, v(-117.75, -99.07) * mm, v(-118.45, -98.57) * mm, v(-120.1, -98.48) * mm, v(-124.23, -98.62) * mm, v(-127.68, -98.92) * mm, v(-134.57, -100.24) * mm, v(-142, -101.94) * mm, v(-147.26, -103.08) * mm, v(-153.8, -104.52) * mm, v(-162.96, -106.15) * mm, v(-168.76, -106.85) * mm, v(-173.91, -107.15) * mm, v(-181.25, -107.3) * mm, v(-186.15, -107.05) * mm, v(-190.42, -106.84) * mm, v(-194.22, -106.37) * mm, v(-197.63, -105.8) * mm, v(-200.82, -105.36) * mm, v(-201.97, -105.2) * mm, v(-202.45, -105.15) * mm, v(-202.73, -105.25) * mm, v(-202.88, -105.35) * mm, v(-202.88, -105.5) * mm], "startDerivative": vector(-11.95, 38.51) * mm, "endDerivative": vector(2.6, -17.78) * mm});
            skFitSpline(sketch, "E186", {"points": [v(-199.86, -114.76) * mm, v(-195.32, -114.91) * mm, v(-192.21, -114.87) * mm, v(-188.48, -114.7) * mm, v(-183.43, -114.5) * mm, v(-177.98, -113.96) * mm, v(-170.85, -113.29) * mm, v(-162.52, -112.33) * mm, v(-156.02, -111.54) * mm, v(-151.73, -111.08) * mm, v(-145.64, -110.66) * mm, v(-140.77, -110.37) * mm, v(-133.8, -110.08) * mm, v(-128.27, -110.08) * mm, v(-122.93, -110.5) * mm, v(-119.73, -111.11) * mm], "startDerivative": vector(77.16, -3.3) * mm, "endDerivative": vector(56.56, -12.62) * mm});
            skFitSpline(sketch, "E187", {"points": [v(-204.13, -99.36) * mm, v(-203.92, -101.07) * mm, v(-203.87, -101.33) * mm, v(-203.73, -101.57) * mm, v(-203.45, -101.79) * mm, v(-200.27, -102.62) * mm, v(-195.9, -103.63) * mm, v(-191.66, -104.46) * mm, v(-187.66, -105.15) * mm, v(-183.4, -105.8) * mm, v(-178.8, -106.08) * mm, v(-173.93, -106.37) * mm, v(-168.9, -106.19) * mm, v(-161.17, -105.65) * mm], "startDerivative": vector(4.48, -35.82) * mm, "endDerivative": vector(65.82, 4.7) * mm});
            skFitSpline(sketch, "E188", {"points": [v(-204.13, -99.36) * mm, v(-204.13, -99.03) * mm, v(-203.92, -98.57) * mm, v(-203.48, -98.3) * mm, v(-202.98, -98.35) * mm, v(-201.97, -98.7) * mm, v(-200.13, -99.44) * mm, v(-196.97, -100.56) * mm, v(-192.97, -101.8) * mm, v(-188.96, -102.76) * mm, v(-183.01, -103.95) * mm, v(-178.5, -104.8) * mm, v(-173.94, -105.36) * mm, v(-171.34, -105.63) * mm, v(-168.82, -105.75) * mm, v(-165.72, -105.73) * mm, v(-161.17, -105.65) * mm], "startDerivative": vector(-1.3, 13.7) * mm, "endDerivative": vector(55.49, 1.12) * mm});
            skLineSegment(sketch, "E189", {"start": v(-50.9, -83.27) * mm, "end": v(-49.42, -75.8) * mm});
            skLineSegment(sketch, "E190", {"start": v(-74.47, -107.4) * mm, "end": v(-75.38, -115.24) * mm});
            skLineSegment(sketch, "E191", {"start": v(-44.91, -108.52) * mm, "end": v(-44.91, -85.81) * mm});
            skLineSegment(sketch, "E192", {"start": v(-44.91, -85.81) * mm, "end": v(-37.35, -85.81) * mm});
            skLineSegment(sketch, "E193", {"start": v(-20.83, -85.81) * mm, "end": v(-20.83, -117.24) * mm});
            skLineSegment(sketch, "E194", {"start": v(-20.83, -117.24) * mm, "end": v(-28.11, -117.24) * mm});
            skLineSegment(sketch, "E195", {"start": v(-28.11, -117.24) * mm, "end": v(-28.11, -113.62) * mm});
            skLineSegment(sketch, "E196", {"start": v(-37.35, -85.81) * mm, "end": v(-37.35, -108.52) * mm});
            skLineSegment(sketch, "E197", {"start": v(-28.51, -85.81) * mm, "end": v(-28.51, -107.83) * mm});
            skLineSegment(sketch, "E198.trimOffspring", {"start": v(-28.51, -85.81) * mm, "end": v(-20.83, -85.81) * mm});
            skLineSegment(sketch, "E199", {"start": v(-16.13, -117.58) * mm, "end": v(-8.7, -117.58) * mm});
            skLineSegment(sketch, "E200", {"start": v(-16.13, -117.58) * mm, "end": v(-16.13, -85.81) * mm});
            skLineSegment(sketch, "E201", {"start": v(-8.7, -117.58) * mm, "end": v(-8.7, -95.34) * mm});
            skLineSegment(sketch, "E202", {"start": v(0.23, -117.58) * mm, "end": v(0.23, -95.57) * mm});
            skLineSegment(sketch, "E203", {"start": v(8.03, -117.58) * mm, "end": v(8.03, -95.8) * mm});
            skLineSegment(sketch, "E204", {"start": v(12.75, -117.58) * mm, "end": v(12.75, -73.3) * mm});
            skLineSegment(sketch, "E205", {"start": v(12.75, -73.3) * mm, "end": v(36.33, -73.3) * mm});
            skLineSegment(sketch, "E206", {"start": v(36.33, -73.3) * mm, "end": v(36.33, -80.13) * mm});
            skLineSegment(sketch, "E207", {"start": v(36.33, -80.13) * mm, "end": v(20.82, -80.13) * mm});
            skLineSegment(sketch, "E208", {"start": v(20.82, -80.13) * mm, "end": v(20.82, -90.8) * mm});
            skLineSegment(sketch, "E209", {"start": v(20.82, -110.61) * mm, "end": v(37.05, -110.61) * mm});
            skLineSegment(sketch, "E210", {"start": v(37.05, -110.61) * mm, "end": v(37.05, -117.58) * mm});
            skLineSegment(sketch, "E211", {"start": v(20.82, -90.8) * mm, "end": v(33.19, -90.8) * mm});
            skLineSegment(sketch, "E212", {"start": v(33.19, -90.8) * mm, "end": v(33.19, -98.13) * mm});
            skLineSegment(sketch, "E213", {"start": v(33.19, -98.13) * mm, "end": v(20.82, -98.13) * mm});
            skLineSegment(sketch, "E214", {"start": v(39.8, -85.81) * mm, "end": v(48.94, -101.48) * mm});
            skLineSegment(sketch, "E215", {"start": v(48.24, -85.81) * mm, "end": v(53.28, -94.3) * mm});
            skLineSegment(sketch, "E216", {"start": v(58.42, -85.81) * mm, "end": v(53.28, -94.3) * mm});
            skLineSegment(sketch, "E217", {"start": v(66.62, -85.81) * mm, "end": v(57.3, -101.08) * mm});
            skLineSegment(sketch, "E218", {"start": v(69.47, -85.81) * mm, "end": v(69.47, -130.56) * mm});
            skLineSegment(sketch, "E219", {"start": v(69.47, -130.56) * mm, "end": v(77.25, -130.56) * mm});
            skLineSegment(sketch, "E220", {"start": v(77.25, -130.56) * mm, "end": v(77.25, -114.65) * mm});
            skLineSegment(sketch, "E221", {"start": v(98.22, -117.58) * mm, "end": v(98.22, -85.81) * mm});
            skFitSpline(sketch, "E222", {"points": [v(-49.42, -75.8) * mm, v(-51.45, -74.53) * mm, v(-54.78, -73.34) * mm, v(-58.99, -72.6) * mm, v(-63.75, -72.85) * mm, v(-67.01, -73.83) * mm, v(-70.16, -75.8) * mm, v(-73.21, -79.12) * mm, v(-74.5, -82.84) * mm, v(-74.47, -87.22) * mm, v(-73.84, -90.3) * mm, v(-72.1, -93.2) * mm, v(-69.78, -95.27) * mm, v(-68.03, -96.5) * mm, v(-65.08, -98.15) * mm, v(-61.16, -99.97) * mm, v(-58.18, -102) * mm, v(-57.06, -103.26) * mm, v(-56.57, -105.2) * mm, v(-56.67, -107.96) * mm, v(-58, -109.71) * mm, v(-60.18, -110.94) * mm, v(-63.09, -111.5) * mm, v(-66.77, -111.11) * mm, v(-69.99, -109.89) * mm, v(-72.37, -108.7) * mm, v(-74.47, -107.4) * mm], "startDerivative": vector(-56.48, 39.34) * mm, "endDerivative": vector(-61.2, 39.37) * mm});
            skPoint(sketch, "E223.13.internal.snap0", {"position": v(-44.91, -97.16) * mm});
            skFitSpline(sketch, "E223", {"points": [v(-75.38, -115.24) * mm, v(-73.1, -116.33) * mm, v(-70.58, -117.2) * mm, v(-66.59, -118.12) * mm, v(-63.4, -118.12) * mm, v(-59.3, -117.75) * mm, v(-54.8, -116.37) * mm, v(-52.11, -114.47) * mm, v(-50.07, -112.26) * mm, v(-48.8, -109.71) * mm, v(-48.17, -105.6) * mm, v(-48.23, -102.18) * mm, v(-49.14, -99.32) * mm, v(-50.38, -97.16) * mm, v(-52.65, -95.02) * mm, v(-54.83, -93.64) * mm, v(-58, -92.04) * mm, v(-61.02, -90.54) * mm, v(-63.7, -88.98) * mm, v(-65.05, -87.95) * mm, v(-66.23, -86.36) * mm, v(-66.3, -83.53) * mm, v(-65, -81.26) * mm, v(-63.08, -80) * mm, v(-60.22, -79.67) * mm, v(-57.75, -79.88) * mm, v(-55.12, -80.7) * mm, v(-53.09, -81.8) * mm, v(-50.9, -83.27) * mm], "startDerivative": vector(69.03, -35.17) * mm, "endDerivative": vector(65.6, -46.07) * mm});
            skFitSpline(sketch, "E224", {"points": [v(-44.91, -108.52) * mm, v(-44.7, -110.95) * mm, v(-43.83, -113.66) * mm, v(-42.12, -116.15) * mm, v(-40.35, -117.32) * mm, v(-38.2, -118) * mm, v(-36.56, -118.08) * mm, v(-33.99, -118.06) * mm, v(-31.95, -117.3) * mm, v(-29.68, -115.55) * mm, v(-28.11, -113.62) * mm], "startDerivative": vector(1.16, -24) * mm, "endDerivative": vector(13.97, 19.41) * mm});
            skFitSpline(sketch, "E225", {"points": [v(-37.35, -108.52) * mm, v(-36.93, -109.52) * mm, v(-36.06, -110.87) * mm, v(-34.51, -111.75) * mm, v(-32.38, -111.76) * mm, v(-30.9, -110.92) * mm, v(-29.17, -109.01) * mm, v(-28.51, -107.83) * mm], "startDerivative": vector(3.25, -8.47) * mm, "endDerivative": vector(4.12, 8.7) * mm});
            skFitSpline(sketch, "E226", {"points": [v(-8.7, -95.34) * mm, v(-8.25, -94.3) * mm, v(-6.69, -92.39) * mm, v(-4.9, -91.24) * mm, v(-3.42, -91.15) * mm, v(-1.86, -91.56) * mm, v(-0.59, -92.8) * mm, v(0, -94.27) * mm, v(0.23, -95.57) * mm], "startDerivative": vector(3.22, 9.32) * mm, "endDerivative": vector(1.58, -11.57) * mm});
            skFitSpline(sketch, "E227", {"points": [v(-8.7, -88.92) * mm, v(-7.83, -87.82) * mm, v(-6.13, -86.33) * mm, v(-4.26, -85.3) * mm, v(-3.07, -84.92) * mm, v(-1.76, -84.93) * mm, v(0.62, -84.97) * mm, v(2.03, -85.33) * mm, v(4.12, -86.3) * mm, v(5.67, -87.78) * mm, v(6.97, -90.05) * mm, v(7.73, -92.71) * mm, v(8.03, -95.8) * mm], "startDerivative": vector(11.21, 15.5) * mm, "endDerivative": vector(1.97, -30.63) * mm});
            skLineSegment(sketch, "E228.trimOffspring", {"start": v(-8.7, -88.92) * mm, "end": v(-8.7, -85.81) * mm});
            skLineSegment(sketch, "E229.trimOffspring", {"start": v(0.23, -117.58) * mm, "end": v(8.03, -117.58) * mm});
            skLineSegment(sketch, "E230.trimOffspring", {"start": v(39.8, -85.81) * mm, "end": v(48.24, -85.81) * mm});
            skLineSegment(sketch, "E231.trimOffspring", {"start": v(12.75, -117.58) * mm, "end": v(37.05, -117.58) * mm});
            skLineSegment(sketch, "E232.trimOffspring", {"start": v(20.82, -98.13) * mm, "end": v(20.82, -110.61) * mm});
            skLineSegment(sketch, "E233.trimOffspring", {"start": v(39.2, -117.58) * mm, "end": v(47.21, -117.58) * mm});
            skLineSegment(sketch, "E234.trimOffspring", {"start": v(52.9, -108.27) * mm, "end": v(58.32, -117.58) * mm});
            skLineSegment(sketch, "E235.trimOffspring", {"start": v(48.94, -101.48) * mm, "end": v(39.2, -117.58) * mm});
            skLineSegment(sketch, "E236.trimOffspring", {"start": v(57.3, -101.08) * mm, "end": v(67.08, -117.58) * mm});
            skLineSegment(sketch, "E237.trimOffspring", {"start": v(52.9, -108.27) * mm, "end": v(47.21, -117.58) * mm});
            skLineSegment(sketch, "E238.trimOffspring", {"start": v(58.42, -85.81) * mm, "end": v(66.62, -85.81) * mm});
            skLineSegment(sketch, "E239.trimOffspring", {"start": v(58.32, -117.58) * mm, "end": v(67.08, -117.58) * mm});
            skFitSpline(sketch, "E240", {"points": [v(77.25, -93.72) * mm, v(78.24, -92.24) * mm, v(79.84, -91.25) * mm, v(81.98, -91.16) * mm, v(84.03, -91.88) * mm, v(85.55, -93.52) * mm, v(86.46, -95.65) * mm, v(86.92, -98.32) * mm, v(87.2, -101.25) * mm, v(87.05, -104.37) * mm, v(86.63, -106.71) * mm, v(85.5, -109.41) * mm, v(84.28, -110.89) * mm, v(83.15, -111.68) * mm, v(82.4, -111.96) * mm, v(81.47, -112) * mm, v(80.82, -111.94) * mm, v(79.66, -111.5) * mm, v(77.99, -110.06) * mm, v(77.42, -109.49) * mm, v(77.25, -108.7) * mm], "startDerivative": vector(17.59, 31.04) * mm, "endDerivative": vector(-2.64, 25.67) * mm});
            skLineSegment(sketch, "E241.trimOffspring", {"start": v(77.25, -87.9) * mm, "end": v(77.25, -85.81) * mm});
            skFitSpline(sketch, "E242", {"points": [v(77.25, -87.9) * mm, v(78.15, -86.92) * mm, v(79.06, -86.1) * mm, v(80.6, -85.27) * mm, v(82.33, -84.95) * mm, v(84.87, -84.9) * mm, v(87.1, -85.42) * mm, v(89.23, -86.4) * mm, v(91.61, -88.78) * mm, v(93.47, -92.1) * mm, v(94.74, -97.44) * mm, v(94.86, -101.98) * mm, v(94.7, -105.96) * mm, v(93.76, -110.32) * mm, v(92.2, -113.53) * mm, v(90.11, -116.06) * mm, v(86.18, -117.97) * mm, v(83.85, -118.07) * mm, v(81.33, -117.99) * mm, v(79.18, -116.95) * mm, v(77.83, -115.84) * mm, v(77.25, -114.65) * mm], "startDerivative": vector(27.64, 30.32) * mm, "endDerivative": vector(-13.67, 37.9) * mm});
            skLineSegment(sketch, "E243.trimOffspring", {"start": v(98.22, -85.81) * mm, "end": v(105.55, -85.81) * mm});
            skLineSegment(sketch, "E244.trimOffspring", {"start": v(98.22, -117.58) * mm, "end": v(105.81, -117.58) * mm});
            skLineSegment(sketch, "E245", {"start": v(105.81, -117.58) * mm, "end": v(105.81, -96.32) * mm});
            skLineSegment(sketch, "E246", {"start": v(105.55, -90.54) * mm, "end": v(105.55, -85.81) * mm});
            skLineSegment(sketch, "E247", {"start": v(115, -92.16) * mm, "end": v(115.6, -85.2) * mm});
            skLineSegment(sketch, "E248", {"start": v(123.16, -97.56) * mm, "end": v(132, -97.56) * mm});
            skLineSegment(sketch, "E249", {"start": v(139.12, -102.83) * mm, "end": v(123.28, -102.83) * mm});
            skLineSegment(sketch, "E250", {"start": v(138.55, -109.28) * mm, "end": v(139.05, -115.3) * mm});
            skLineSegment(sketch, "E251", {"start": v(141.83, -115.8) * mm, "end": v(142.97, -109.21) * mm});
            skLineSegment(sketch, "E252", {"start": v(161.17, -93.3) * mm, "end": v(162.04, -86.8) * mm});
            skLineSegment(sketch, "E253", {"start": v(69.47, -85.81) * mm, "end": v(77.25, -85.81) * mm});
            skLineSegment(sketch, "E254", {"start": v(-8.7, -85.81) * mm, "end": v(-16.13, -85.81) * mm});
            skLineSegment(sketch, "E255", {"start": v(77.25, -93.72) * mm, "end": v(77.25, -108.7) * mm});
            skFitSpline(sketch, "E256", {"points": [v(105.55, -90.54) * mm, v(106.34, -88.95) * mm, v(107.88, -87.04) * mm, v(111.21, -85.33) * mm, v(113.92, -85.12) * mm, v(115.6, -85.2) * mm], "startDerivative": vector(4.23, 9.16) * mm, "endDerivative": vector(9.52, -0.55) * mm});
            skFitSpline(sketch, "E257", {"points": [v(105.81, -96.32) * mm, v(107.09, -94.41) * mm, v(108.75, -92.95) * mm, v(111.55, -91.95) * mm, v(113.55, -91.79) * mm, v(115, -92.16) * mm], "startDerivative": vector(5.94, 9.67) * mm, "endDerivative": vector(8.5, -2.82) * mm});
            skFitSpline(sketch, "E258", {"points": [v(138.55, -109.28) * mm, v(135.58, -110.84) * mm, v(133.58, -111.6) * mm, v(131.1, -111.72) * mm, v(128.51, -111.37) * mm, v(125.56, -109.28) * mm, v(124.03, -106.6) * mm, v(123.28, -102.83) * mm], "startDerivative": vector(-20.74, -11.05) * mm, "endDerivative": vector(-3.6, 24.4) * mm});
            skFitSpline(sketch, "E259", {"points": [v(132, -97.56) * mm, v(132, -95.66) * mm, v(131.34, -92.98) * mm, v(129.6, -90.84) * mm, v(127.85, -90.54) * mm, v(125.89, -91.12) * mm, v(124.25, -92.9) * mm, v(123.43, -95.76) * mm, v(123.16, -97.56) * mm], "startDerivative": vector(0.7, 15.96) * mm, "endDerivative": vector(-1.95, -14.92) * mm});
            skFitSpline(sketch, "E260", {"points": [v(139.12, -102.83) * mm, v(139.35, -99.78) * mm, v(139.12, -94.3) * mm, v(137.79, -90.24) * mm, v(135.16, -87.15) * mm, v(132.15, -85.48) * mm, v(129.19, -84.94) * mm, v(126.7, -84.9) * mm, v(123.56, -85.62) * mm, v(121.07, -86.94) * mm, v(118.74, -89.37) * mm, v(116.83, -92.82) * mm, v(115.8, -96.95) * mm, v(115.39, -101.5) * mm, v(116.17, -107.84) * mm, v(118.15, -112.12) * mm, v(120.83, -115.2) * mm, v(125.88, -117.83) * mm, v(129.76, -118.06) * mm, v(133.16, -117.96) * mm, v(136.53, -116.97) * mm, v(139.05, -115.3) * mm], "startDerivative": vector(6.66, 65.6) * mm, "endDerivative": vector(56.35, 42.66) * mm});
            skFitSpline(sketch, "E261", {"points": [v(162.04, -86.8) * mm, v(158.42, -85.46) * mm, v(153.56, -84.9) * mm, v(149.37, -85.46) * mm, v(146.7, -86.9) * mm, v(144.6, -88.87) * mm, v(143.28, -90.42) * mm, v(142.74, -93.5) * mm, v(142.96, -97.06) * mm, v(144.46, -100.42) * mm, v(146.47, -102.3) * mm, v(149.43, -103.94) * mm, v(152.65, -105.44) * mm, v(154.7, -106.92) * mm, v(155.36, -109.28) * mm, v(154.92, -110.8) * mm, v(153.15, -111.94) * mm, v(150.1, -111.98) * mm, v(146.98, -111.28) * mm, v(143.18, -108.95) * mm, v(143, -109.03) * mm, v(142.97, -109.21) * mm], "startDerivative": vector(-60.25, 26.52) * mm, "endDerivative": vector(-0.78, -15.64) * mm});
            skFitSpline(sketch, "E262", {"points": [v(141.83, -115.8) * mm, v(143.49, -116.64) * mm, v(146.03, -117.43) * mm, v(149.52, -118.13) * mm, v(151.85, -118.08) * mm, v(154.96, -117.92) * mm, v(158.36, -116.8) * mm, v(160.62, -115.3) * mm, v(162.37, -112.72) * mm, v(163.07, -109.59) * mm, v(163.07, -106.68) * mm, v(162.04, -103.46) * mm, v(160.2, -101.15) * mm, v(157.6, -99.34) * mm, v(154.2, -97.56) * mm, v(151.9, -96.62) * mm, v(150.58, -95.45) * mm, v(150.2, -93.8) * mm, v(150.28, -92.88) * mm, v(151.25, -91.61) * mm, v(152.56, -90.92) * mm, v(155.44, -90.87) * mm, v(157.82, -91.49) * mm, v(159.77, -92.36) * mm, v(161.17, -93.3) * mm], "startDerivative": vector(43.99, -24.8) * mm, "endDerivative": vector(38.4, -28.85) * mm});
            skLineSegment(sketch, "E263", {"start": v(164.92, -115.9) * mm, "end": v(166.07, -109.32) * mm});
            skLineSegment(sketch, "E264", {"start": v(184.26, -93.41) * mm, "end": v(185.14, -86.91) * mm});
            skFitSpline(sketch, "E265", {"points": [v(185.14, -86.91) * mm, v(181.52, -85.56) * mm, v(176.66, -85) * mm, v(172.47, -85.57) * mm, v(169.8, -87.02) * mm, v(167.7, -88.98) * mm, v(166.38, -90.52) * mm, v(165.83, -93.6) * mm, v(166.05, -97.17) * mm, v(167.56, -100.53) * mm, v(169.56, -102.4) * mm, v(172.52, -104.05) * mm, v(175.75, -105.55) * mm, v(177.8, -107.02) * mm, v(178.46, -109.39) * mm, v(178.02, -110.91) * mm, v(176.25, -112.05) * mm, v(173.2, -112.1) * mm, v(170.08, -111.38) * mm, v(166.28, -109.06) * mm, v(166.1, -109.13) * mm, v(166.07, -109.32) * mm], "startDerivative": vector(-60.25, 26.52) * mm, "endDerivative": vector(-0.78, -15.64) * mm});
            skFitSpline(sketch, "E266", {"points": [v(164.92, -115.9) * mm, v(166.58, -116.74) * mm, v(169.12, -117.53) * mm, v(172.61, -118.23) * mm, v(174.94, -118.18) * mm, v(178.05, -118.03) * mm, v(181.45, -116.9) * mm, v(183.71, -115.41) * mm, v(185.47, -112.83) * mm, v(186.16, -109.7) * mm, v(186.16, -106.78) * mm, v(185.14, -103.56) * mm, v(183.29, -101.26) * mm, v(180.69, -99.45) * mm, v(177.3, -97.67) * mm, v(174.99, -96.72) * mm, v(173.68, -95.56) * mm, v(173.3, -93.9) * mm, v(173.38, -92.98) * mm, v(174.35, -91.72) * mm, v(175.66, -91.03) * mm, v(178.53, -90.98) * mm, v(180.91, -91.6) * mm, v(182.87, -92.46) * mm, v(184.26, -93.41) * mm], "startDerivative": vector(43.99, -24.8) * mm, "endDerivative": vector(38.4, -28.85) * mm});
            skLineSegment(sketch, "E267", {"start": v(-137.44, -59.31) * mm, "end": v(-137.45, -59.32) * mm});
            skSolve(sketch);
        }
        {
            var Q0;
            Q0 = qSketchRegion(id + "F27", true);
            extrude(context, id + "F28", {"entities" : qUnion([Q0]), "operationType" : NewBodyOperationType.REMOVE, "oppositeDirection" : true, "depth" : 5 * mm});
        }
    });
